# Revit family: Plumbing-Sink-Sloan-Valve-EW-42000
name_source: partatom
category: Plumbing Fixtures
units: mm (PartAtom-declared; Revit-internal decimal feet)

## family parameters
Cut with Voids When Loaded = No
Host = Face
OmniClass Number = 23.45.05.14.14
OmniClass Title = Sinks/Lavatories
Part Type = Normal
Room Calculation Point = No
Round Connector Dimension = Use Diameter
Shared = No

## types (1)
- EW-42000
    Apparent Load = 688 VA
    Assembly Code = D2010400
    CW Connection = Yes
    CWFU = 1.5
    Cold Water Connection Diameter = 1/2"
    Current = 15 A
    Default Elevation = 0"
    Depth = 21"
    Description = SloanStone® 2-Station Wall-Mounted Washstation Sink.
    Edition number = 1
    Frequency = 60 Hz
    HW Connection = Yes
    HWFU = 1.5
    Height = 21 1/2"
    Hot Water Connection Diameter = 1/2"
    Keynote = 10000
    Manufacturer = Sloan Valve
    Model = EW-42000
    Number of Poles = 3
    Power Factor = 0.8
    Product Material = Sloan - SloanStone - Pearl (PL)
    Product data url = https://bimobject.com
    Sanitary Drain Connection Diameter = 1 1/2"
    URL = www.sloanvalve.com
    Valve Pressure Drop = 0.0 Pa
    Vent Connection = No
    Voltage = 110 V
    WFU = 2
    Waste Connection = Yes
    Water Flow = 0.5 GPM
    Width = 54 3/4"

## geometry (parser evidence)
native form markers: Sweep x3
no freeform markers — native parametric forms only
